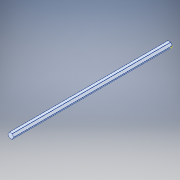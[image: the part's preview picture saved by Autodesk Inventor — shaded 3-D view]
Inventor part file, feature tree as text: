
AUTODESK INVENTOR PART (.ipt)
format: ipt  version: 2017 (Build 210142000, 142)  size: 157,696 bytes
history: native  units: in
note: dims shown in document units (in); Inventor stores cm internally (conversion verified against a paired STEP export)
features: sketch x6, split x1, fillet x1
ambient origin geometry x8: Origin, YZ Plane, XZ Plane, XY Plane, X Axis, Y Axis, Z Axis, Center Point
bodies: Solid1 (feature_tree)
feature tree (8):
  sketch  "Sketch1"  dims[d11=16.0in]
  split  "Split1"
  sketch  "Sketch3"  dims[d13=7.8125in]
  sketch  "Sketch4"  dims[d14=3.5453in]
  sketch  "Sketch5"  dims[d15=3.5453in]
  sketch  "Sketch7"
  sketch  "Sketch2"  dims[d12=7.8125in]
  fillet  "Fillet1"  Radius=8.5in
